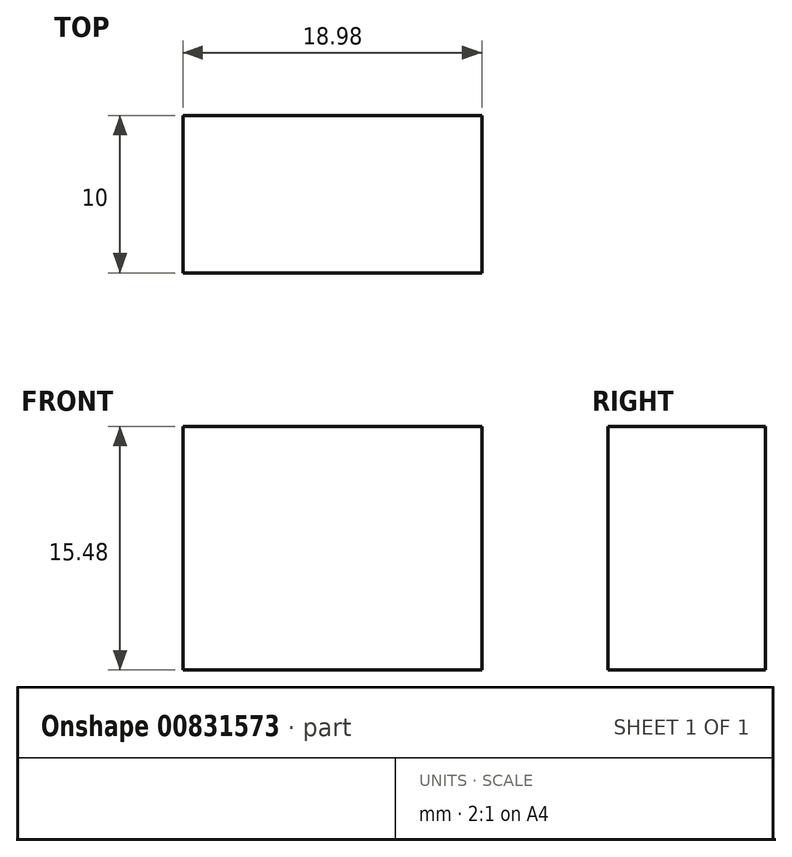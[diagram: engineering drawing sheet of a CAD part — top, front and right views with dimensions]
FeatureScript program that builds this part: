
annotation { "Feature Type Name" : "Feature", "Feature Type Description" : "" }
export const myFeature = defineFeature(function(context is Context, id is Id, definition is map)
    precondition{}
    {
        {
            var Q0;
            Q0=qCreatedBy(makeId("Front.planeOp"),FACE);
            var sketch = newSketch(context, id + "F0", { "sketchPlane" : qUnion([Q0])});
            skLineSegment(sketch, "E0.bottom", {"start": v(-9.5, 7.74) * mm, "end": v(9.5, 7.74) * mm});
            skLineSegment(sketch, "E0.top", {"start": v(-9.5, -7.74) * mm, "end": v(9.5, -7.74) * mm});
            skLineSegment(sketch, "E0.left", {"start": v(-9.5, 7.74) * mm, "end": v(-9.5, -7.74) * mm});
            skLineSegment(sketch, "E0.right", {"start": v(9.5, 7.74) * mm, "end": v(9.5, -7.74) * mm});
            skPoint(sketch, "E0.middle", {"position": v(0, 0) * mm});
            skSolve(sketch);
        }
        {
            var Q0;
            Q0 = qSketchRegion(id + "F0", true);
            extrude(context, id + "F1", {"entities" : qUnion([Q0]), "depth" : 10 * mm, "offsetDistance" : 25.4 * mm});
        }
    });
